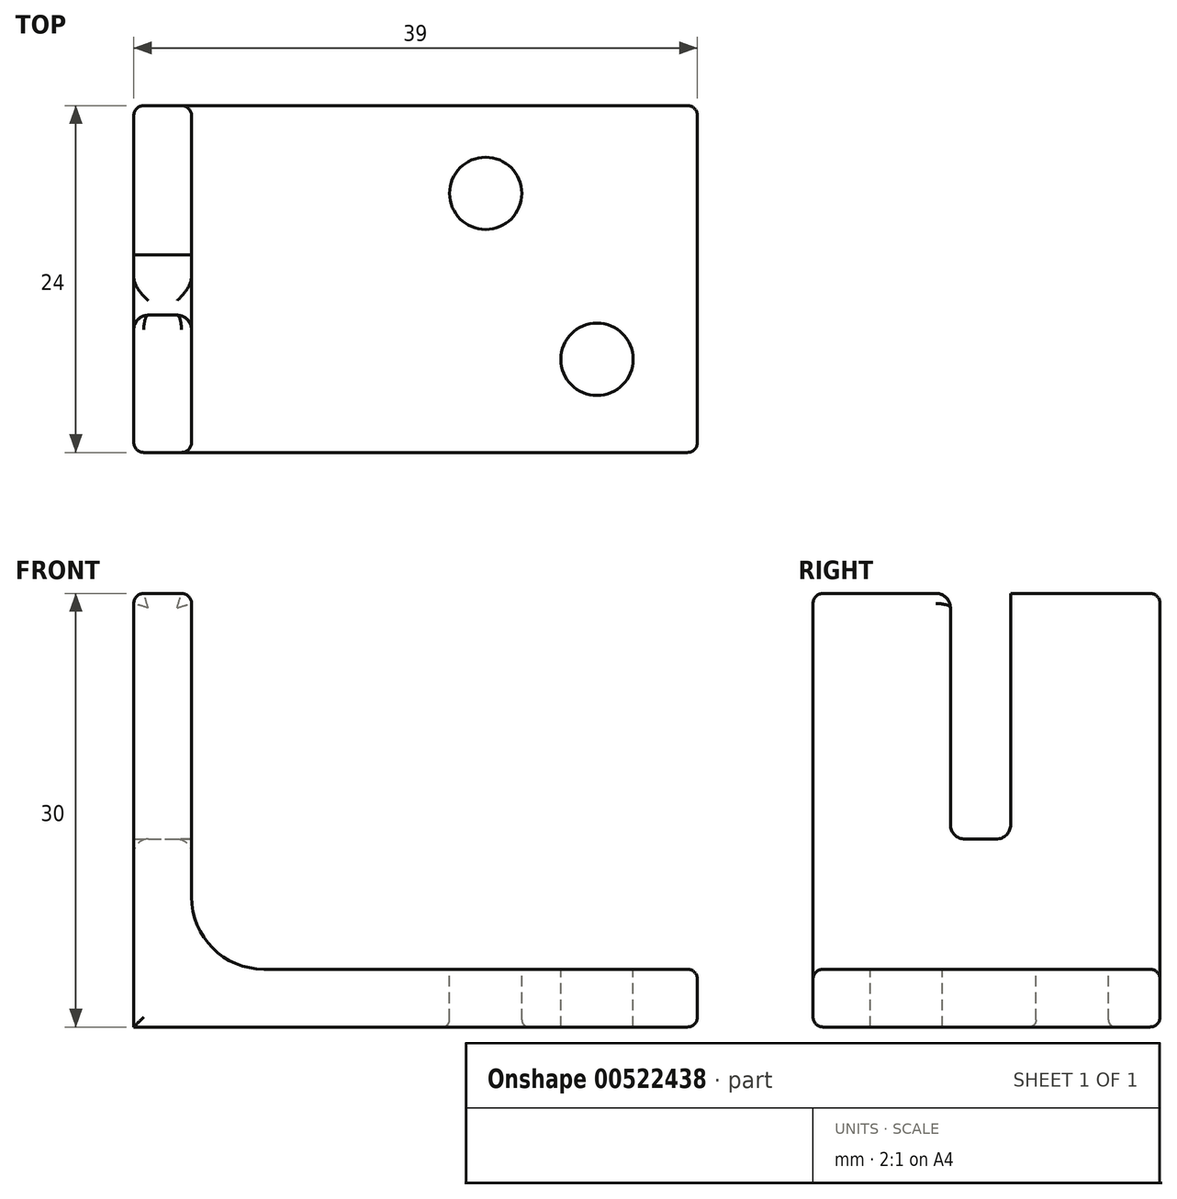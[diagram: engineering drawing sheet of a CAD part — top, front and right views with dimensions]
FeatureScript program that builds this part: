
annotation { "Feature Type Name" : "Feature", "Feature Type Description" : "" }
export const myFeature = defineFeature(function(context is Context, id is Id, definition is map)
    precondition{}
    {
        {
            var Q0;
            Q0=qCreatedBy(makeId("Front.planeOp"),FACE);
            var sketch = newSketch(context, id + "F0", { "sketchPlane" : qUnion([Q0])});
            skLineSegment(sketch, "E0", {"start": v(-35, 4) * mm, "end": v(-35, 30) * mm});
            skLineSegment(sketch, "E1.0", {"start": v(-39, 0) * mm, "end": v(-39, 30) * mm});
            skLineSegment(sketch, "E2.0", {"start": v(0, 4) * mm, "end": v(-35, 4) * mm});
            skLineSegment(sketch, "E3", {"start": v(-39, 30) * mm, "end": v(-35, 30) * mm});
            skLineSegment(sketch, "E4", {"start": v(0, 0) * mm, "end": v(0, 4) * mm});
            skLineSegment(sketch, "E5", {"start": v(-39, 0) * mm, "end": v(0, 0) * mm});
            skSolve(sketch);
        }
        {
            var Q0;
            Q0=qSketchRegion(id+"F0",true);
            var Q1;
            Q1=makeQuery(id+"F0.imprint","IMPRINT",FACE,{"disambiguationData":[TD([[makeQuery(id+"F0.imprint","IMPRINT",EDGE,{"derivedFrom":sQuery(id+"F0.wireOp",EDGE,"E0")}),1.0]])]});
            extrude(context, id + "F1", {"entities" : qUnion([Q0, Q1]), "oppositeDirection" : true, "depth" : 24 * mm, "offsetDistance" : 25 * mm});
        }
        {
            var Q0;
            Q0=makeQuery(id+"F1.opExtrude","SWEPT_FACE",FACE,{"disambiguationData":[OSD([sQuery(id+"F0.wireOp",EDGE,"E2.0")])]});
            var sketch = newSketch(context, id + "F2", { "sketchPlane" : qUnion([Q0])});
            skCircle(sketch, "E6", {"center": v(-14.65, 17.93) * mm, "radius": 2.5 * mm});
            skCircle(sketch, "E7", {"center": v(-6.95, 6.45) * mm, "radius": 2.5 * mm});
            skSolve(sketch);
        }
        {
            var Q0;
            Q0=qSketchRegion(id+"F2",true);
            extrude(context, id + "F3", {"entities" : qUnion([Q0]), "operationType" : NewBodyOperationType.REMOVE, "oppositeDirection" : true, "depth" : 25 * mm, "offsetDistance" : 25 * mm});
        }
        {
            var Q0;
            Q0=makeQuery(id+"F1.opExtrude","SWEPT_FACE",FACE,{"disambiguationData":[OSD([sQuery(id+"F0.wireOp",EDGE,"E0")])]});
            var sketch = newSketch(context, id + "F4", { "sketchPlane" : qUnion([Q0])});
            skPoint(sketch, "E8.center.orphan", {"position": v(11.5, 20) * mm});
            skLineSegment(sketch, "E9", {"start": v(13.67, 30) * mm, "end": v(13.67, 13) * mm});
            skLineSegment(sketch, "E10", {"start": v(13.67, 13) * mm, "end": v(9.5, 13) * mm});
            skLineSegment(sketch, "E11", {"start": v(9.5, 13) * mm, "end": v(9.5, 30) * mm});
            skSolve(sketch);
        }
        {
            var Q0;
            Q0=makeQuery(id+"F1.opExtrude","SWEPT_EDGE",EDGE,{"disambiguationData":[OSD([sQuery(id+"F0.wireOp",EDGE,"E0"),sQuery(id+"F0.wireOp",EDGE,"E2.0")])]});
            fillet(context, id + "F5", {"entities" : qUnion([Q0]), "radius" : 5 * mm, "tangentPropagation" : true, "allowEdgeOverflow" : false});
        }
        {
            var Q0;
            Q0=makeQuery(id+"F1.opExtrude","SWEPT_FACE",FACE,{"disambiguationData":[OSD([sQuery(id+"F0.wireOp",EDGE,"E3")])]});
            var Q1;
            Q1=makeQuery(id+"F1.opExtrude","CAP_FACE",FACE,{"disambiguationData":[OSD([sQuery(id+"F0.wireOp",EDGE,"E0"),sQuery(id+"F0.wireOp",EDGE,"E1.0"),sQuery(id+"F0.wireOp",EDGE,"E2.0"),sQuery(id+"F0.wireOp",EDGE,"E3"),sQuery(id+"F0.wireOp",EDGE,"E4"),sQuery(id+"F0.wireOp",EDGE,"E5")])],"isStart":true});
            var Q2;
            Q2=makeQuery(id+"F1.opExtrude","SWEPT_FACE",FACE,{"disambiguationData":[OSD([sQuery(id+"F0.wireOp",EDGE,"E4")])]});
            var Q3;
            Q3=makeQuery(id+"F1.opExtrude","CAP_FACE",FACE,{"disambiguationData":[OSD([sQuery(id+"F0.wireOp",EDGE,"E0"),sQuery(id+"F0.wireOp",EDGE,"E1.0"),sQuery(id+"F0.wireOp",EDGE,"E2.0"),sQuery(id+"F0.wireOp",EDGE,"E3"),sQuery(id+"F0.wireOp",EDGE,"E4"),sQuery(id+"F0.wireOp",EDGE,"E5")])],"isStart":false});
            fillet(context, id + "F6", {"entities" : qUnion([Q0, Q1, Q2, Q3]), "radius" : .7 * mm, "tangentPropagation" : true, "allowEdgeOverflow" : false});
        }
        {
            var Q0;
            Q0=makeQuery(id+"F3.boolean.opBoolean","INTERSECT",EDGE,{"derivedFrom":[makeQuery(id+"F1.opExtrude","SWEPT_FACE",FACE,{"disambiguationData":[OSD([sQuery(id+"F0.wireOp",EDGE,"E5")])]}),makeQuery(id+"F3.opExtrude","SWEPT_FACE",FACE,{"disambiguationData":[OSD([sQuery(id+"F2.wireOp",EDGE,"E6")])]})]});
            var Q1;
            Q1=makeQuery(id+"F3.boolean.opBoolean","COPY",EDGE,{"derivedFrom":makeQuery(id+"F3.opExtrude","CAP_EDGE",EDGE,{"disambiguationData":[OSD([sQuery(id+"F2.wireOp",EDGE,"E7")])],"isStart":true})});
            var Q2;
            Q2=makeQuery(id+"F3.boolean.opBoolean","COPY",EDGE,{"derivedFrom":makeQuery(id+"F3.opExtrude","CAP_EDGE",EDGE,{"disambiguationData":[OSD([sQuery(id+"F2.wireOp",EDGE,"E6")])],"isStart":true})});
            var Q3;
            Q3=makeQuery(id+"FW94dfINJSYCeAk_1.boolean.opBoolean","COPY",FACE,{"derivedFrom":makeQuery(id+"FW94dfINJSYCeAk_1.opExtrude","SWEPT_FACE",FACE,{"disambiguationData":[OSD([sQuery(id+"F4.wireOp",EDGE,"E8")])]})});
            fillet(context, id + "F7", {"entities" : qUnion([Q0, Q1, Q2, Q3]), "radius" : .5 * mm, "tangentPropagation" : true, "allowEdgeOverflow" : false});
        }
        {
            var Q0;
            Q0 = qSketchRegion(id + "F4", true);
            var Q1;
            {var subQ0=sQuery(id+"F4.wireOp",EDGE,"E9");Q1=makeQuery(id+"F4.imprint","IMPRINT",FACE,{"disambiguationData":[TD([[makeQuery(id+"F4.imprint","IMPRINT",EDGE,{"derivedFrom":subQ0}),-1.0]])]});}
            extrude(context, id + "F8", {"entities" : qUnion([Q0, Q1]), "operationType" : NewBodyOperationType.REMOVE, "oppositeDirection" : true, "depth" : 25 * mm, "offsetDistance" : 25 * mm});
        }
        {
            var Q0;
            Q0=makeQuery(id+"F8.boolean.opBoolean","COPY",EDGE,{"derivedFrom":makeQuery(id+"F8.opExtrude","SWEPT_EDGE",EDGE,{"disambiguationData":[OSD([sQuery(id+"F0.wireOp",EDGE,"E0"),sQuery(id+"F0.wireOp",EDGE,"E3"),sQuery(id+"F4.wireOp",EDGE,"E9")])]})});
            var Q1;
            Q1=makeQuery(id+"F8.boolean.opBoolean","COPY",EDGE,{"derivedFrom":makeQuery(id+"F8.opExtrude","SWEPT_EDGE",EDGE,{"disambiguationData":[OSD([sQuery(id+"F0.wireOp",EDGE,"E0"),sQuery(id+"F0.wireOp",EDGE,"E3"),sQuery(id+"F4.wireOp",EDGE,"E11")])]})});
            var Q2;
            Q2=makeQuery(id+"F8.boolean.opBoolean","COPY",EDGE,{"derivedFrom":makeQuery(id+"F8.opExtrude","SWEPT_EDGE",EDGE,{"disambiguationData":[OSD([sQuery(id+"F4.wireOp",EDGE,"E10"),sQuery(id+"F4.wireOp",EDGE,"E11")])]})});
            var Q3;
            Q3=makeQuery(id+"F8.boolean.opBoolean","COPY",EDGE,{"derivedFrom":makeQuery(id+"F8.opExtrude","SWEPT_EDGE",EDGE,{"disambiguationData":[OSD([sQuery(id+"F4.wireOp",EDGE,"E9"),sQuery(id+"F4.wireOp",EDGE,"E10")])]})});
            fillet(context, id + "F9", {"entities" : qUnion([Q0, Q1, Q2, Q3]), "radius" : 1 * mm, "tangentPropagation" : true, "allowEdgeOverflow" : false});
        }
    });
